# Revit family: DF_СчетчикУдаровМолнии_FOREND_91887_EZETEK
name_source: partatom
category: Соединительные детали воздуховодов
revit_build: Autodesk Revit 2017 (Build: 20170118_1100(x64)
units: mm (PartAtom-declared; Revit-internal decimal feet)

## family parameters
Всегда вертикально = Да
На основе рабочей плоскости = Нет
Общий = Нет
При загрузке вырезать с полостями = Нет
Размер круглого соединителя = Использовать радиус
Тип детали = Соединение

## types (1)
- СчетчикУдаровМолнии_FOREND_91887
    ADSK_Версия Revit = 2017
    ADSK_Единица измерения = Неспецифицируемое
    ADSK_Завод-изготовитель = Неспецифицируемое
    ADSK_Код изделия = Неспецифицируемое
    ADSK_Количество = 0
    ADSK_Марка = Неспецифицируемое
    ADSK_Масса = 0
    ADSK_Масса_Текст = Неспецифицируемое
    ADSK_Материал = BIMLIB_Сталь_Оцинкованная_EZETEK
    ADSK_Наименование = Неспецифицируемое
    ADSK_Обозначение = Неспецифицируемое
    URL = https://ezetek.ru
    Группа модели = Активная молниезащита
    Изготовитель = Ezetek
    Описание = Держатель выполнен из оцинкованной стали и применяется для закрепления полосы и прутка на горизонтальных и вертикальных поверхностях. Зажим стягивается болтами с гайками М8. Для крепления держатель имеет отверстие диаметром 8,4 мм под винт либо саморез.
    Тип = FA_СчетчикУдаровМолнии_FOREND_91887_EZETEK : СчетчикУдаровМолнии_FOREND_91887
    Угол = 90.00°
